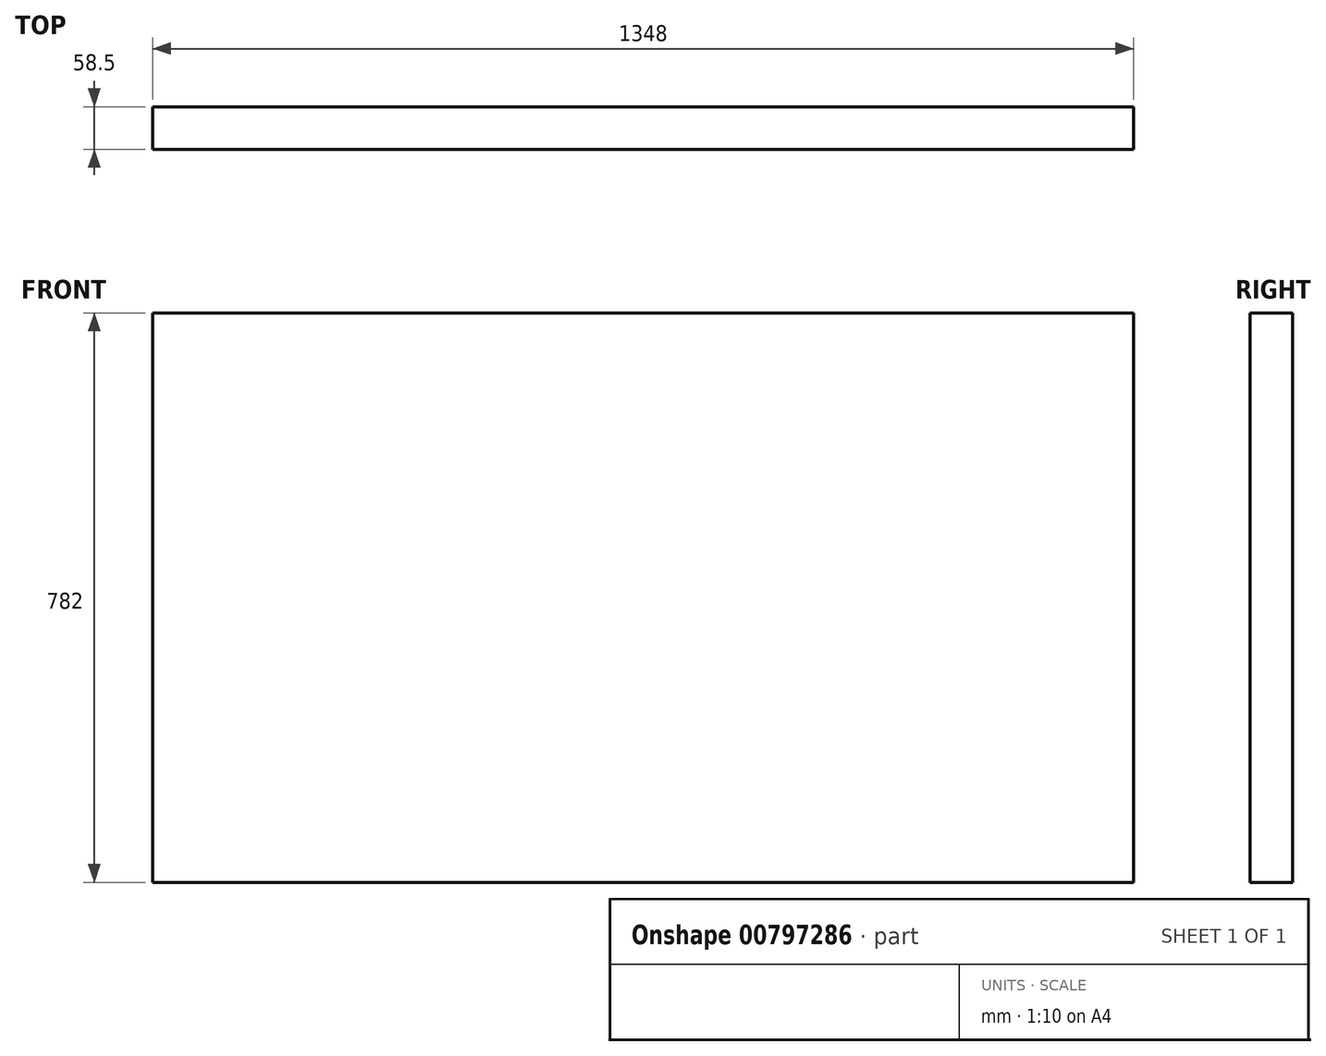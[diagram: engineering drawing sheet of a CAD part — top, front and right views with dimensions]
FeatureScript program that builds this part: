
annotation { "Feature Type Name" : "Feature", "Feature Type Description" : "" }
export const myFeature = defineFeature(function(context is Context, id is Id, definition is map)
    precondition{}
    {
        {
            var Q0;
            Q0=qCreatedBy(makeId("Front.planeOp"),FACE);
            var sketch = newSketch(context, id + "F0", { "sketchPlane" : qUnion([Q0])});
            skLineSegment(sketch, "E0.bottom", {"start": v(674, 391) * mm, "end": v(-674, 391) * mm});
            skLineSegment(sketch, "E0.top", {"start": v(674, -391) * mm, "end": v(-674, -391) * mm});
            skLineSegment(sketch, "E0.left", {"start": v(674, 391) * mm, "end": v(674, -391) * mm});
            skLineSegment(sketch, "E0.right", {"start": v(-674, 391) * mm, "end": v(-674, -391) * mm});
            skPoint(sketch, "E0.middle", {"position": v(0, 0) * mm});
            skSolve(sketch);
        }
        {
            var Q0;
            Q0 = qSketchRegion(id + "F0", true);
            extrude(context, id + "F1", {"entities" : qUnion([Q0]), "depth" : 58.5 * mm, "offsetDistance" : 25 * mm, "symmetric" : true});
        }
    });
